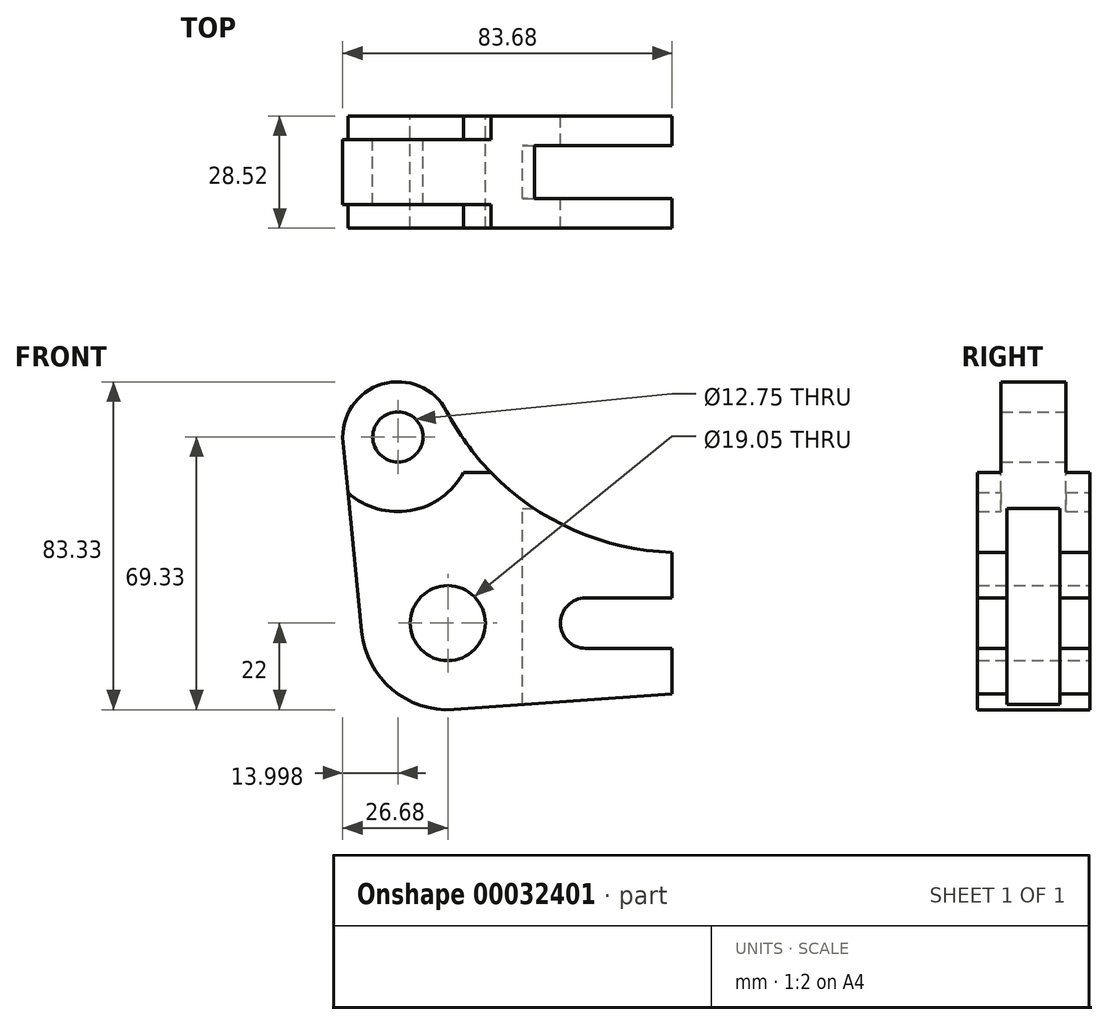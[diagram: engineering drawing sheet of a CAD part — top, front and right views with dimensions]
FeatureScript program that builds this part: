
annotation { "Feature Type Name" : "Feature", "Feature Type Description" : "" }
export const myFeature = defineFeature(function(context is Context, id is Id, definition is map)
    precondition{}
    {
        {
            var Q0;
            Q0=qCreatedBy(makeId("Front.planeOp"),FACE);
            var sketch = newSketch(context, id + "F0", { "sketchPlane" : qUnion([Q0])});
            skArc(sketch, "E0", {"start": v(-21.9, -2.15) * mm, "mid": v(-14.19, -16.81) * mm, "end": v(1.56, -21.94) * mm});
            skLineSegment(sketch, "E1", {"start": v(57, -6.38) * mm, "end": v(35, -6.38) * mm});
            skLineSegment(sketch, "E2", {"start": v(35, 6.38) * mm, "end": v(57, 6.38) * mm});
            skLineSegment(sketch, "E3", {"start": v(57, 6.38) * mm, "end": v(57, 18) * mm});
            skLineSegment(sketch, "E4", {"start": v(57, -6.38) * mm, "end": v(57, -18) * mm});
            skLineSegment(sketch, "E5", {"start": v(1.56, -21.94) * mm, "end": v(57, -18) * mm});
            skLineSegment(sketch, "E6", {"start": v(0, 0) * mm, "end": v(35, 0) * mm, "construction": true});
            skArc(sketch, "E7", {"start": v(35, 6.38) * mm, "mid": v(28.63, 0) * mm, "end": v(35, -6.38) * mm});
            skArc(sketch, "E8", {"start": v(-0.29, 53.84) * mm, "mid": v(-16.7, 60.74) * mm, "end": v(-26.62, 45.96) * mm});
            skLineSegment(sketch, "E9", {"start": v(0, 0) * mm, "end": v(-12.68, 47.33) * mm, "construction": true});
            skLineSegment(sketch, "E10", {"start": v(-21.9, -2.15) * mm, "end": v(-26.62, 45.96) * mm});
            skArc(sketch, "E11", {"start": v(-0.29, 53.84) * mm, "mid": v(23.5, 28.17) * mm, "end": v(57, 18) * mm});
            skArc(sketch, "E12", {"start": v(-25.36, 33.18) * mm, "mid": v(-9.4, 28.62) * mm, "end": v(4.05, 38.33) * mm});
            skCircle(sketch, "E13", {"center": v(-12.68, 47.33) * mm, "radius": 6.38 * mm});
            skCircle(sketch, "E14", {"center": v(0, 0) * mm, "radius": 9.53 * mm});
            skLineSegment(sketch, "E15", {"start": v(4.05, 38.33) * mm, "end": v(10.94, 38.33) * mm});
            skSolve(sketch);
        }
        {
            var Q0;
            {var subQ3=sQuery(id+"F0.wireOp",EDGE,"E8");Q0=makeQuery(id+"F0.imprint","IMPRINT",FACE,{"disambiguationData":[TD([[makeQuery(id+"F0.imprint","IMPRINT",EDGE,{"derivedFrom":subQ3}),1.0]])]});}
            extrude(context, id + "F1", {"entities" : qUnion([Q0]), "endBound" : BoundingType.SYMMETRIC, "depth" : 16.52 * mm});
        }
        {
            var Q0;
            {var subQ5=sQuery(id+"F0.wireOp",EDGE,"E0");Q0=makeQuery(id+"F0.imprint","IMPRINT",FACE,{"disambiguationData":[TD([[makeQuery(id+"F0.imprint","IMPRINT",EDGE,{"derivedFrom":subQ5}),1.0]])]});}
            extrude(context, id + "F2", {"entities" : qUnion([Q0]), "operationType" : NewBodyOperationType.ADD, "endBound" : BoundingType.SYMMETRIC, "depth" : 28.52 * mm});
        }
        {
            var Q0;
            Q0=makeQuery(id+"F2.opExtrude","SWEPT_FACE",FACE,{"disambiguationData":[OSD([sQuery(id+"F0.wireOp",EDGE,"E3")])]});
            var sketch = newSketch(context, id + "F3", { "sketchPlane" : qUnion([Q0])});
            skLineSegment(sketch, "E16.bottom", {"start": v(-6.74, -29.36) * mm, "end": v(6.74, -29.36) * mm});
            skLineSegment(sketch, "E16.top", {"start": v(-6.75, 29.13) * mm, "end": v(6.75, 29.13) * mm});
            skLineSegment(sketch, "E16.left", {"start": v(-6.74, -29.36) * mm, "end": v(-6.75, 29.13) * mm});
            skLineSegment(sketch, "E16.right", {"start": v(6.75, -29.36) * mm, "end": v(6.74, 29.13) * mm});
            skLineSegment(sketch, "E17", {"start": v(0, -29.36) * mm, "end": v(0, -22.11) * mm, "construction": true});
            skSolve(sketch);
        }
        {
            var Q0;
            Q0 = qSketchRegion(id + "F3", true);
            extrude(context, id + "F4", {"entities" : qUnion([Q0]), "operationType" : NewBodyOperationType.REMOVE, "oppositeDirection" : true, "depth" : 38 * mm});
        }
    });
